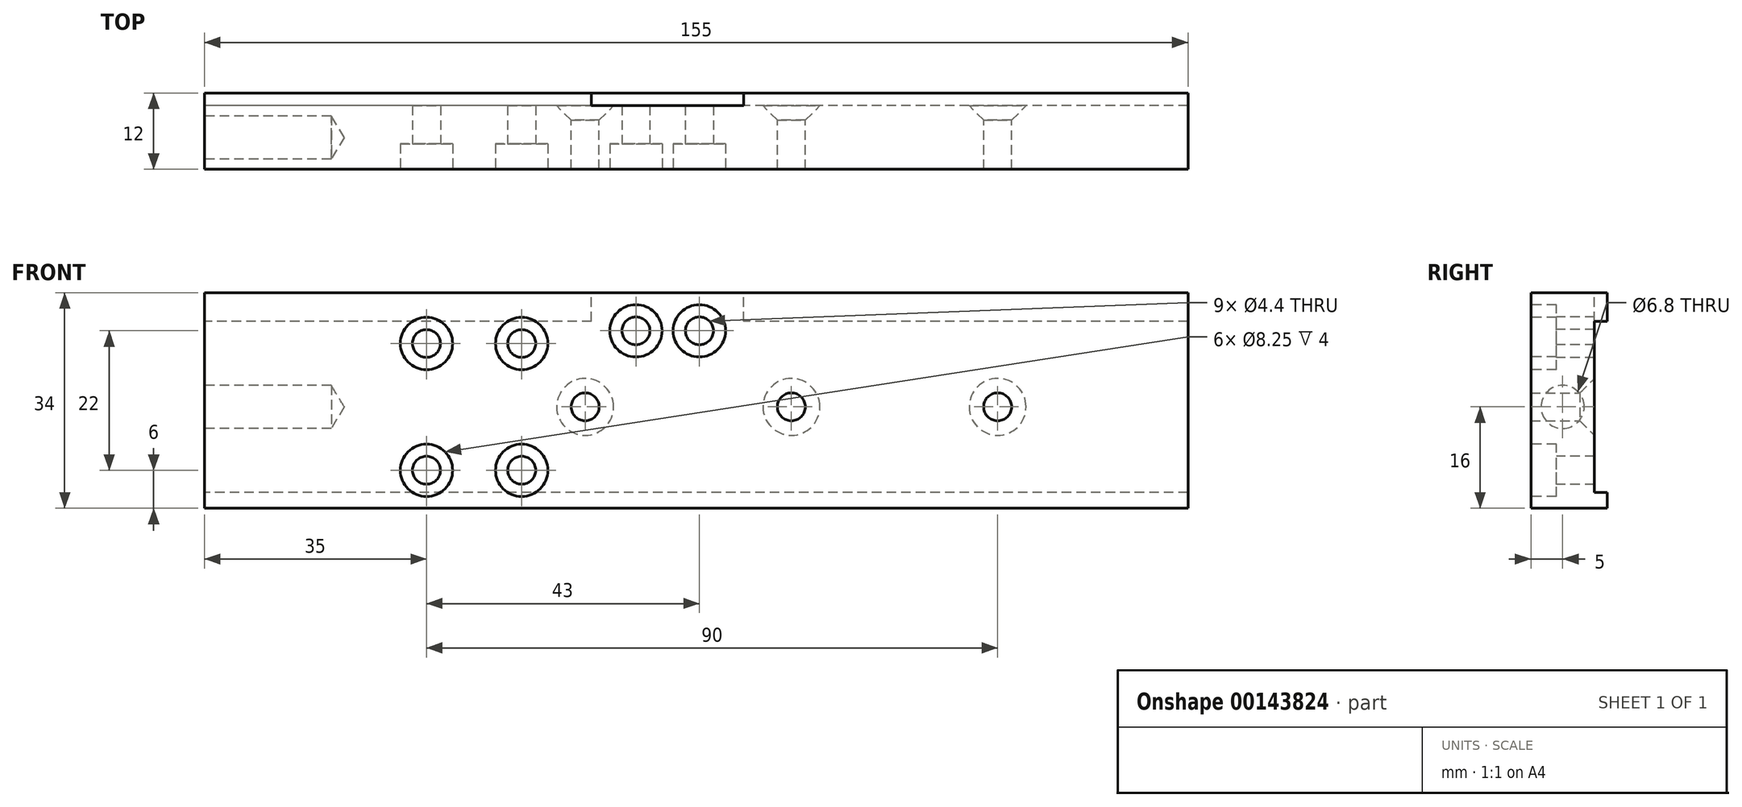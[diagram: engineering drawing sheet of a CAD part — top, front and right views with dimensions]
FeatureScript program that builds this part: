
annotation { "Feature Type Name" : "Feature", "Feature Type Description" : "" }
export const myFeature = defineFeature(function(context is Context, id is Id, definition is map)
    precondition{}
    {
        {
            var Q0;
            Q0=qCreatedBy(makeId("Front.planeOp"),FACE);
            var sketch = newSketch(context, id + "F0", { "sketchPlane" : qUnion([Q0])});
            skLineSegment(sketch, "E0.bottom", {"start": v(77.5, -17) * mm, "end": v(-77.5, -17) * mm});
            skLineSegment(sketch, "E0.top", {"start": v(77.5, 17) * mm, "end": v(-77.5, 17) * mm});
            skLineSegment(sketch, "E0.left", {"start": v(77.5, -17) * mm, "end": v(77.5, 17) * mm});
            skLineSegment(sketch, "E0.right", {"start": v(-77.5, -17) * mm, "end": v(-77.5, 17) * mm});
            skPoint(sketch, "E0.middle", {"position": v(0, 0) * mm});
            skSolve(sketch);
        }
        {
            var Q0;
            Q0=makeQuery(id+"F0.imprint","IMPRINT",FACE,{"disambiguationData":[TD([[makeQuery(id+"F0.imprint","IMPRINT",EDGE,{"derivedFrom":sQuery(id+"F0.wireOp",EDGE,"E0.bottom")}),-1.0]])]});
            extrude(context, id + "F1", {"entities" : qUnion([Q0]), "depth" : 10 * mm});
        }
        {
            var Q0;
            Q0=makeQuery(id+"F1.opExtrude","CAP_FACE",FACE,{"disambiguationData":[OSD([sQuery(id+"F0.wireOp",EDGE,"E0.bottom"),sQuery(id+"F0.wireOp",EDGE,"E0.top"),sQuery(id+"F0.wireOp",EDGE,"E0.left"),sQuery(id+"F0.wireOp",EDGE,"E0.right")])],"isStart":true});
            var sketch = newSketch(context, id + "F2", { "sketchPlane" : qUnion([Q0])});
            skLineSegment(sketch, "E1", {"start": v(-77.5, 12.5) * mm, "end": v(-7.5, 12.5) * mm});
            skLineSegment(sketch, "E2", {"start": v(-77.5, -14.5) * mm, "end": v(77.5, -14.5) * mm});
            skLineSegment(sketch, "E3", {"start": v(-7.5, 12.5) * mm, "end": v(-7.5, 17) * mm});
            skLineSegment(sketch, "E4", {"start": v(16.5, 12.5) * mm, "end": v(16.5, 17) * mm});
            skLineSegment(sketch, "E5.trimOffspring", {"start": v(16.5, 12.5) * mm, "end": v(77.5, 12.5) * mm});
            skSolve(sketch);
        }
        {
            var Q0;
            {var subQ0=sQuery(id+"F2.wireOp",EDGE,"E4");Q0=makeQuery(id+"F2.imprint","IMPRINT",FACE,{"disambiguationData":[TD([[makeQuery(id+"F2.imprint","IMPRINT",EDGE,{"derivedFrom":subQ0}),-1.0]])]});}
            var Q1;
            {var subQ0=sQuery(id+"F2.wireOp",EDGE,"E1");Q1=makeQuery(id+"F2.imprint","IMPRINT",FACE,{"disambiguationData":[TD([[makeQuery(id+"F2.imprint","IMPRINT",EDGE,{"derivedFrom":subQ0}),1.0]])]});}
            var Q2;
            {var subQ0=sQuery(id+"F2.wireOp",EDGE,"E2");Q2=makeQuery(id+"F2.imprint","IMPRINT",FACE,{"disambiguationData":[TD([[makeQuery(id+"F2.imprint","IMPRINT",EDGE,{"derivedFrom":subQ0}),-1.0]])]});}
            extrude(context, id + "F3", {"entities" : qUnion([Q0, Q1, Q2]), "operationType" : NewBodyOperationType.ADD, "depth" : 2 * mm});
        }
        {
            var Q0;
            Q0=makeQuery(id+"F1.opExtrude","CAP_FACE",FACE,{"disambiguationData":[OSD([sQuery(id+"F0.wireOp",EDGE,"E0.bottom"),sQuery(id+"F0.wireOp",EDGE,"E0.top"),sQuery(id+"F0.wireOp",EDGE,"E0.left"),sQuery(id+"F0.wireOp",EDGE,"E0.right")])],"isStart":false});
            var sketch = newSketch(context, id + "F4", { "sketchPlane" : qUnion([Q0])});
            skCircle(sketch, "E6", {"center": v(-9.5, 11) * mm, "radius": 1.6 * mm});
            skCircle(sketch, "E7", {"center": v(0.5, 11) * mm, "radius": 1.6 * mm});
            skCircle(sketch, "E8", {"center": v(-42.5, 9) * mm, "radius": 1.6 * mm});
            skCircle(sketch, "E9", {"center": v(-27.5, 9) * mm, "radius": 1.6 * mm});
            skCircle(sketch, "E10", {"center": v(-42.5, -11) * mm, "radius": 1.6 * mm});
            skCircle(sketch, "E11", {"center": v(-27.5, -11) * mm, "radius": 1.6 * mm});
            skSolve(sketch);
        }
        {
            var Q0;
            Q0=sQuery(id+"F4.wireOp",VERTEX,"E8.center");
            var Q1;
            Q1=sQuery(id+"F4.wireOp",VERTEX,"E9.center");
            var Q2;
            Q2=sQuery(id+"F4.wireOp",VERTEX,"E6.center");
            var Q3;
            Q3=sQuery(id+"F4.wireOp",VERTEX,"E7.center");
            var Q4;
            Q4=sQuery(id+"F4.wireOp",VERTEX,"E11.center");
            var Q5;
            Q5=sQuery(id+"F4.wireOp",VERTEX,"E10.center");
            var Q6;
            Q6=makeQuery(id+"F1.opExtrude","SWEPT_BODY",BODY,{"disambiguationData":[OSD([sQuery(id+"F0.wireOp",EDGE,"E0.bottom"),sQuery(id+"F0.wireOp",EDGE,"E0.top"),sQuery(id+"F0.wireOp",EDGE,"E0.left"),sQuery(id+"F0.wireOp",EDGE,"E0.right")])]});
            hole(context, id + "F5", {"style" : HoleStyle.C_BORE, "endStyle" : HoleEndStyle.THROUGH, "standardTappedOrClearance" : lookupTablePath({ "standard" : "ISO", "fit" : "Normal", "size" : "M4", "type" : "Clearance" }), "standardBlindInLast" : lookupTablePath({ "fit" : "Standard", "standard" : "ISO", "size" : "M4", "type" : "Clearance" }), "holeDiameter" : 4.4 * mm, "cBoreDiameter" : 8.25 * mm, "cBoreDepth" : 4 * mm, "startFromSketch" : true, "locations" : qUnion([Q0, Q1, Q2, Q3, Q4, Q5]), "scope" : qUnion([Q6]), "isTappedThrough" : true});
        }
        {
            var Q0;
            Q0=makeQuery(id+"F1.opExtrude","CAP_FACE",FACE,{"disambiguationData":[OSD([sQuery(id+"F0.wireOp",EDGE,"E0.bottom"),sQuery(id+"F0.wireOp",EDGE,"E0.top"),sQuery(id+"F0.wireOp",EDGE,"E0.left"),sQuery(id+"F0.wireOp",EDGE,"E0.right")])],"isStart":true});
            var sketch = newSketch(context, id + "F6", { "sketchPlane" : qUnion([Q0])});
            skCircle(sketch, "E12", {"center": v(-47.5, -1) * mm, "radius": 1.6 * mm});
            skCircle(sketch, "E13", {"center": v(-15, -1) * mm, "radius": 1.6 * mm});
            skCircle(sketch, "E14", {"center": v(17.5, -1) * mm, "radius": 1.6 * mm});
            skSolve(sketch);
        }
        {
            var Q0;
            Q0=sQuery(id+"F6.wireOp",VERTEX,"E12.center");
            var Q1;
            Q1=sQuery(id+"F6.wireOp",VERTEX,"E13.center");
            var Q2;
            Q2=sQuery(id+"F6.wireOp",VERTEX,"E14.center");
            var Q3;
            Q3=makeQuery(id+"F1.opExtrude","SWEPT_BODY",BODY,{"disambiguationData":[OSD([sQuery(id+"F0.wireOp",EDGE,"E0.bottom"),sQuery(id+"F0.wireOp",EDGE,"E0.top"),sQuery(id+"F0.wireOp",EDGE,"E0.left"),sQuery(id+"F0.wireOp",EDGE,"E0.right")])]});
            hole(context, id + "F7", {"style" : HoleStyle.C_SINK, "endStyle" : HoleEndStyle.THROUGH, "standardTappedOrClearance" : lookupTablePath({ "standard" : "ISO", "fit" : "Normal", "size" : "M4", "type" : "Clearance" }), "standardBlindInLast" : lookupTablePath({ "fit" : "Standard", "standard" : "ISO", "size" : "M4", "type" : "Clearance" }), "holeDiameter" : 4.4 * mm, "cSinkDiameter" : 8.96 * mm, "cSinkAngle" : 90 * degree, "startFromSketch" : true, "locations" : qUnion([Q0, Q1, Q2]), "scope" : qUnion([Q3]), "isTappedThrough" : true});
        }
        {
            var Q0;
            {var subQ0=sQuery(id+"F0.wireOp",EDGE,"E0.right");var subQ1=makeQuery(id+"F1.opExtrude","CAP_EDGE",EDGE,{"disambiguationData":[OSD([subQ0])],"isStart":true});Q0=makeQuery(id+"F3.boolean.opBoolean","MERGE",FACE,{"derivedFrom":[makeQuery(id+"F1.opExtrude","SWEPT_FACE",FACE,{"disambiguationData":[OSD([subQ0])]}),makeQuery(id+"F3.opExtrude","SWEPT_FACE",FACE,{"disambiguationData":[OSD([subQ0]),TDD([makeQuery(id+"F2.imprint","IMPRINT",EDGE,{"disambiguationData":[TD([[makeQuery(id+"F2.imprint","INTERSECT",VERTEX,{"derivedFrom":[makeQuery(id+"F1.opExtrude","CAP_EDGE",EDGE,{"disambiguationData":[OSD([sQuery(id+"F0.wireOp",EDGE,"E0.bottom")])],"isStart":true}),subQ1]}),-1.0]])],"derivedFrom":subQ1})])]}),makeQuery(id+"F3.opExtrude","SWEPT_FACE",FACE,{"disambiguationData":[OSD([subQ0]),TDD([makeQuery(id+"F2.imprint","IMPRINT",EDGE,{"disambiguationData":[TD([[makeQuery(id+"F2.imprint","INTERSECT",VERTEX,{"derivedFrom":[makeQuery(id+"F1.opExtrude","CAP_EDGE",EDGE,{"disambiguationData":[OSD([sQuery(id+"F0.wireOp",EDGE,"E0.top")])],"isStart":true}),subQ1]}),1.0]])],"derivedFrom":subQ1})])]})]});}
            var sketch = newSketch(context, id + "F8", { "sketchPlane" : qUnion([Q0])});
            skCircle(sketch, "E15", {"center": v(5, -1) * mm, "radius": 3.1 * mm});
            skSolve(sketch);
        }
        {
            var Q0;
            Q0=sQuery(id+"F8.wireOp",VERTEX,"E15.center");
            var Q1;
            Q1=makeQuery(id+"F1.opExtrude","SWEPT_BODY",BODY,{"disambiguationData":[OSD([sQuery(id+"F0.wireOp",EDGE,"E0.bottom"),sQuery(id+"F0.wireOp",EDGE,"E0.top"),sQuery(id+"F0.wireOp",EDGE,"E0.left"),sQuery(id+"F0.wireOp",EDGE,"E0.right")])]});
            hole(context, id + "F9", {"style" : HoleStyle.SIMPLE, "endStyle" : HoleEndStyle.BLIND, "standardTappedOrClearance" : lookupTablePath({ "standard" : "ISO", "engagement" : "75%", "pitch" : "1.25 mm", "size" : "M8", "type" : "Tapped" }), "standardBlindInLast" : lookupTablePath({ "standard" : "ISO", "engagement" : "75%", "pitch" : "1.25 mm", "size" : "M8", "type" : "Tapped" }), "holeDiameter" : 6.8 * mm, "holeDepth" : 20 * mm, "startFromSketch" : true, "locations" : qUnion([Q0]), "scope" : qUnion([Q1]), "majorDiameter" : 8 * mm});
        }
    });
